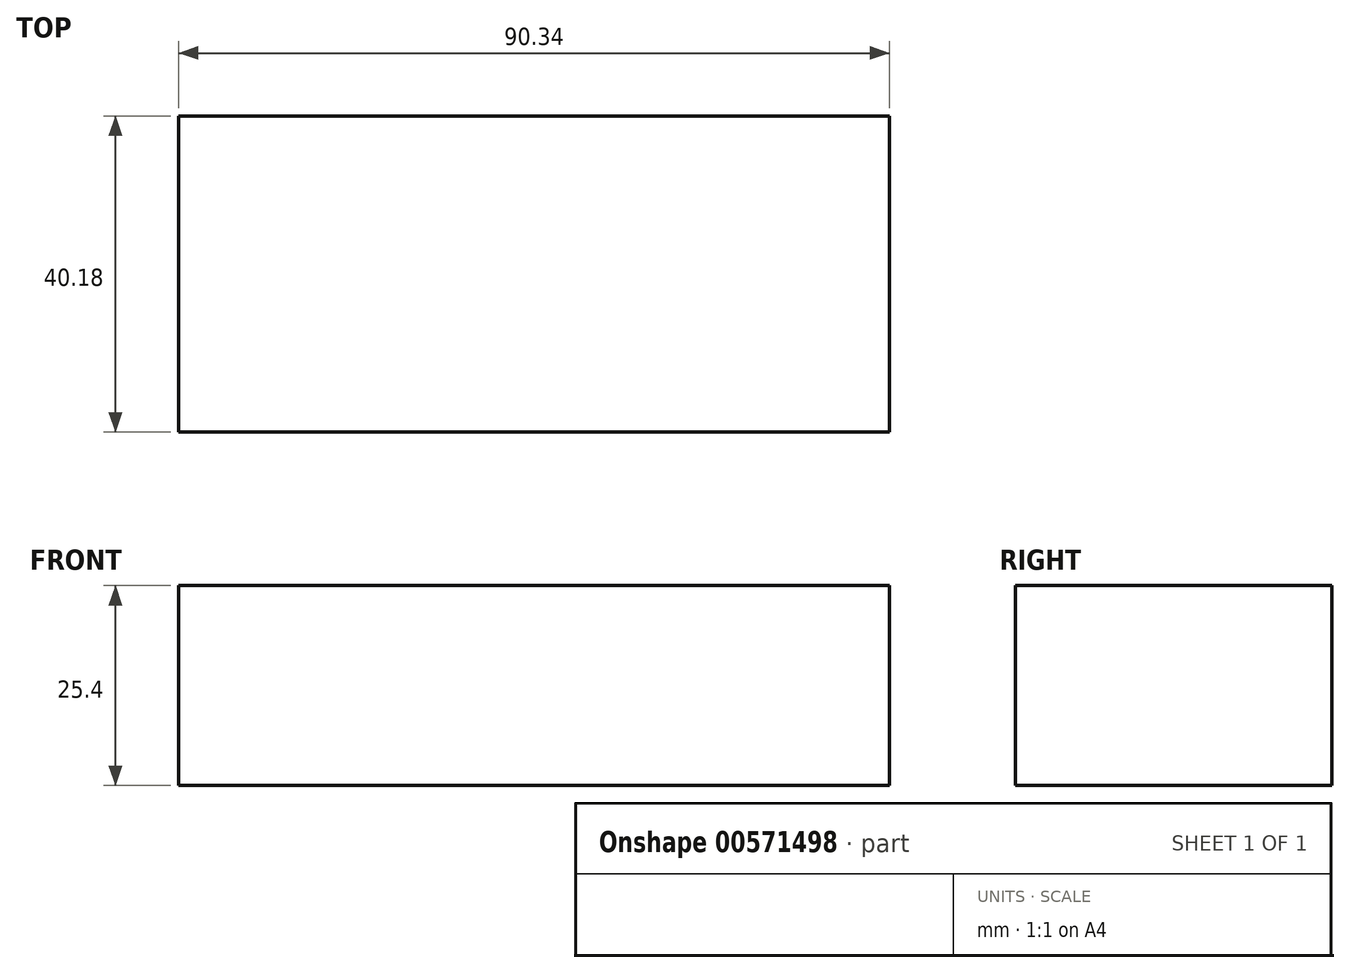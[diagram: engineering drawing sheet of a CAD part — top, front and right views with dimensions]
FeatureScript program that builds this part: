
annotation { "Feature Type Name" : "Feature", "Feature Type Description" : "" }
export const myFeature = defineFeature(function(context is Context, id is Id, definition is map)
    precondition{}
    {
        {
            var Q0;
            Q0=qCreatedBy(makeId("Top.planeOp"),FACE);
            var sketch = newSketch(context, id + "F0", { "sketchPlane" : qUnion([Q0])});
            skLineSegment(sketch, "E0.bottom", {"start": v(-45.17, 20.1) * mm, "end": v(45.17, 20.1) * mm});
            skLineSegment(sketch, "E0.top", {"start": v(-45.17, -20.1) * mm, "end": v(45.17, -20.1) * mm});
            skLineSegment(sketch, "E0.left", {"start": v(-45.17, 20.1) * mm, "end": v(-45.17, -20.1) * mm});
            skLineSegment(sketch, "E0.right", {"start": v(45.17, 20.1) * mm, "end": v(45.17, -20.1) * mm});
            skPoint(sketch, "E0.middle", {"position": v(0, 0) * mm});
            skSolve(sketch);
        }
        {
            var Q0;
            Q0=makeQuery(id+"F0.imprint","IMPRINT",FACE,{"disambiguationData":[TD([[makeQuery(id+"F0.imprint","IMPRINT",EDGE,{"derivedFrom":sQuery(id+"F0.wireOp",EDGE,"E0.bottom")}),-1.0]])]});
            extrude(context, id + "F1", {"entities" : qUnion([Q0]), "depth" : 25.4 * mm, "offsetDistance" : 25.4 * mm});
        }
        {
            var Q0;
            Q0=makeQuery(id+"F1.opExtrude","CAP_FACE",FACE,{"disambiguationData":[OSD([sQuery(id+"F0.wireOp",EDGE,"E0.bottom"),sQuery(id+"F0.wireOp",EDGE,"E0.top"),sQuery(id+"F0.wireOp",EDGE,"E0.left"),sQuery(id+"F0.wireOp",EDGE,"E0.right")])],"isStart":true});
            extrude(context, id + "F2", {"entities" : qUnion([Q0]), "operationType" : NewBodyOperationType.ADD, "oppositeDirection" : true, "depth" : 5.84 * mm, "offsetDistance" : 25.4 * mm, "hasSecondDirection" : true, "secondDirectionOppositeDirection" : true, "secondDirectionDepth" : 3.8 * mm});
        }
    });
